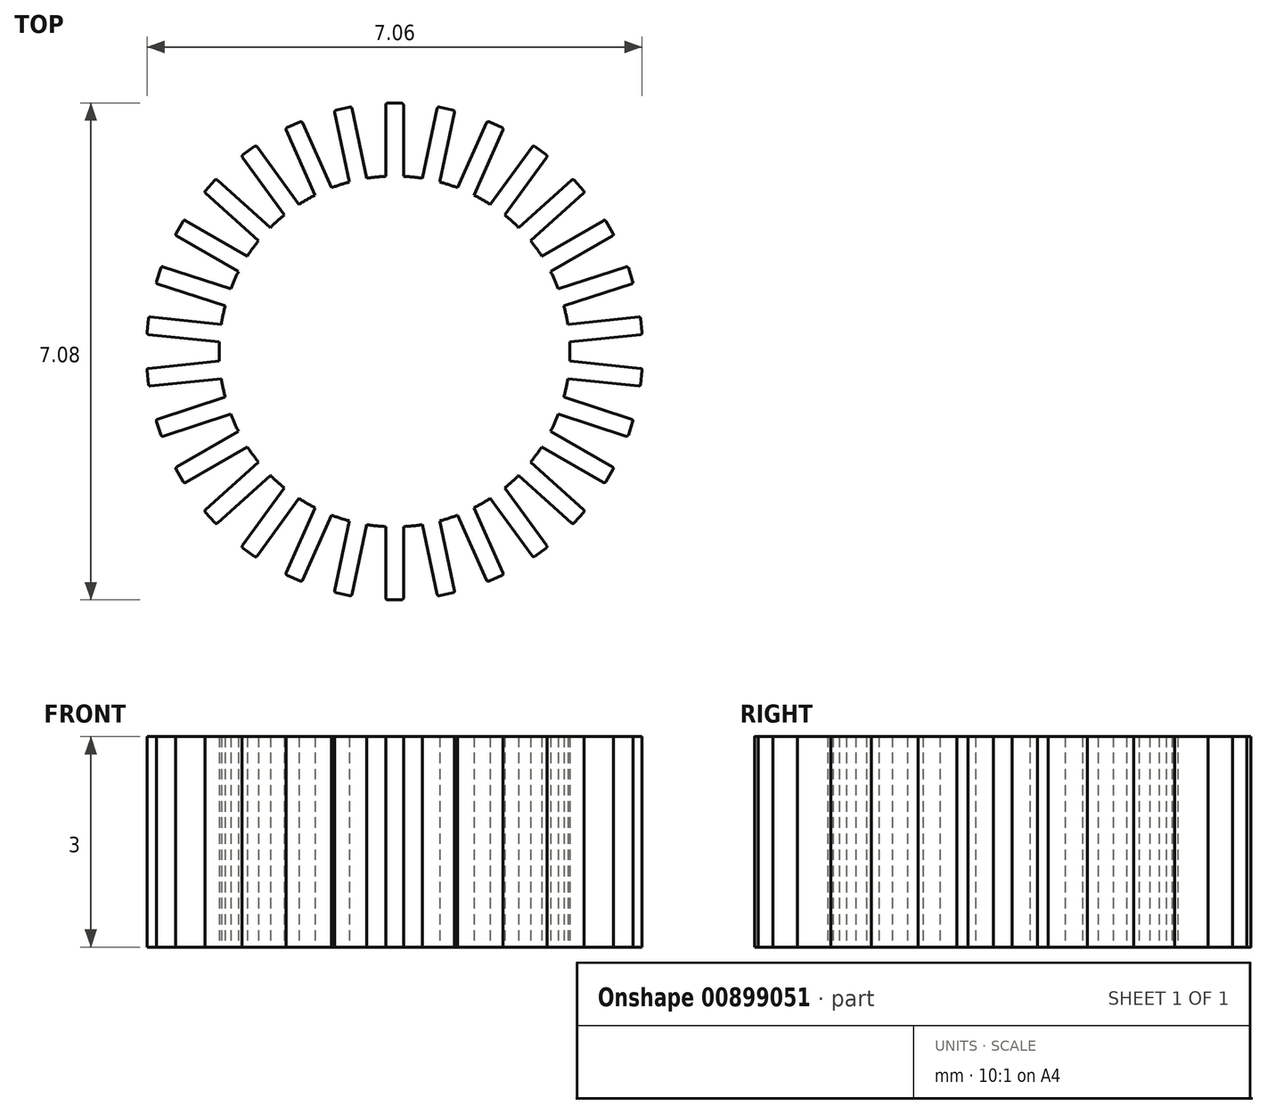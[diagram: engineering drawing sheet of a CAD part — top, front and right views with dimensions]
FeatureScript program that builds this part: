
annotation { "Feature Type Name" : "Feature", "Feature Type Description" : "" }
export const myFeature = defineFeature(function(context is Context, id is Id, definition is map)
    precondition{}
    {
        {
            var Q0;
            Q0=qCreatedBy(makeId("Top.planeOp"),FACE);
            var sketch = newSketch(context, id + "F0", { "sketchPlane" : qUnion([Q0])});
            skCircle(sketch, "E0", {"center": v(0, 0) * mm, "radius": 2.5 * mm});
            skLineSegment(sketch, "E1", {"start": v(0, 3.54) * mm, "end": v(-0.1, 3.54) * mm});
            skLineSegment(sketch, "E2", {"start": v(0, 3.54) * mm, "end": v(0.1, 3.54) * mm});
            skLineSegment(sketch, "E3", {"start": v(-0.13, 3.51) * mm, "end": v(-0.13, 2.5) * mm});
            skLineSegment(sketch, "E4", {"start": v(0.13, 3.51) * mm, "end": v(0.13, 2.5) * mm});
            skPoint(sketch, "E5.visualSharp", {"position": v(-0.13, 3.54) * mm});
            skArc(sketch, "E5.filletArc", {"start": v(-0.1, 3.54) * mm, "mid": v(-0.12, 3.53) * mm, "end": v(-0.13, 3.51) * mm});
            skPoint(sketch, "E6.visualSharp", {"position": v(0.13, 3.54) * mm});
            skArc(sketch, "E6.filletArc", {"start": v(0.13, 3.51) * mm, "mid": v(0.12, 3.53) * mm, "end": v(0.1, 3.54) * mm});
            skLineSegment(sketch, "E7", {"start": v(-0.13, 2.5) * mm, "end": v(-0.05, 2.5) * mm});
            skLineSegment(sketch, "E8.1.0", {"start": v(-2.98, -1.87) * mm, "end": v(-2.1, -1.36) * mm});
            skLineSegment(sketch, "E8.2.0", {"start": v(3.1, -1.65) * mm, "end": v(2.23, -1.14) * mm});
            skArc(sketch, "E9.1.0", {"start": v(-0.84, 3.44) * mm, "mid": v(-0.85, 3.43) * mm, "end": v(-0.85, 3.4) * mm});
            skLineSegment(sketch, "E9.1.1", {"start": v(-0.74, 3.46) * mm, "end": v(-0.84, 3.44) * mm});
            skLineSegment(sketch, "E9.1.2", {"start": v(-0.74, 3.46) * mm, "end": v(-0.64, 3.48) * mm});
            skArc(sketch, "E9.1.3", {"start": v(-0.6, 3.46) * mm, "mid": v(-0.62, 3.48) * mm, "end": v(-0.64, 3.48) * mm});
            skLineSegment(sketch, "E9.1.4", {"start": v(-0.6, 3.46) * mm, "end": v(-0.4, 2.47) * mm});
            skLineSegment(sketch, "E9.1.5", {"start": v(-0.85, 3.4) * mm, "end": v(-0.64, 2.42) * mm});
            skArc(sketch, "E9.2.0", {"start": v(-1.53, 3.2) * mm, "mid": v(-1.55, 3.18) * mm, "end": v(-1.54, 3.16) * mm});
            skLineSegment(sketch, "E9.2.1", {"start": v(-1.44, 3.23) * mm, "end": v(-1.53, 3.2) * mm});
            skLineSegment(sketch, "E9.2.2", {"start": v(-1.44, 3.23) * mm, "end": v(-1.35, 3.27) * mm});
            skArc(sketch, "E9.2.3", {"start": v(-1.31, 3.26) * mm, "mid": v(-1.33, 3.27) * mm, "end": v(-1.35, 3.27) * mm});
            skLineSegment(sketch, "E9.2.4", {"start": v(-1.31, 3.26) * mm, "end": v(-0.9, 2.33) * mm});
            skLineSegment(sketch, "E9.2.5", {"start": v(-1.54, 3.16) * mm, "end": v(-1.13, 2.23) * mm});
            skArc(sketch, "E9.3.0", {"start": v(-2.16, 2.8) * mm, "mid": v(-2.17, 2.79) * mm, "end": v(-2.17, 2.77) * mm});
            skLineSegment(sketch, "E9.3.1", {"start": v(-2.08, 2.86) * mm, "end": v(-2.16, 2.8) * mm});
            skLineSegment(sketch, "E9.3.2", {"start": v(-2.08, 2.86) * mm, "end": v(-2, 2.92) * mm});
            skArc(sketch, "E9.3.3", {"start": v(-1.96, 2.92) * mm, "mid": v(-1.98, 2.93) * mm, "end": v(-2, 2.92) * mm});
            skLineSegment(sketch, "E9.3.4", {"start": v(-1.96, 2.92) * mm, "end": v(-1.36, 2.1) * mm});
            skLineSegment(sketch, "E9.3.5", {"start": v(-2.17, 2.77) * mm, "end": v(-1.57, 1.95) * mm});
            skArc(sketch, "E9.4.0", {"start": v(-2.7, 2.3) * mm, "mid": v(-2.7, 2.27) * mm, "end": v(-2.7, 2.26) * mm});
            skLineSegment(sketch, "E9.4.1", {"start": v(-2.63, 2.37) * mm, "end": v(-2.7, 2.3) * mm});
            skLineSegment(sketch, "E9.4.2", {"start": v(-2.63, 2.37) * mm, "end": v(-2.56, 2.44) * mm});
            skArc(sketch, "E9.4.3", {"start": v(-2.53, 2.44) * mm, "mid": v(-2.54, 2.45) * mm, "end": v(-2.56, 2.44) * mm});
            skLineSegment(sketch, "E9.4.4", {"start": v(-2.53, 2.44) * mm, "end": v(-1.77, 1.77) * mm});
            skLineSegment(sketch, "E9.4.5", {"start": v(-2.7, 2.26) * mm, "end": v(-1.94, 1.58) * mm});
            skArc(sketch, "E9.5.0", {"start": v(-3.11, 1.68) * mm, "mid": v(-3.12, 1.66) * mm, "end": v(-3.1, 1.65) * mm});
            skLineSegment(sketch, "E9.5.1", {"start": v(-3.06, 1.77) * mm, "end": v(-3.11, 1.68) * mm});
            skLineSegment(sketch, "E9.5.2", {"start": v(-3.06, 1.77) * mm, "end": v(-3.01, 1.86) * mm});
            skArc(sketch, "E9.5.3", {"start": v(-2.98, 1.87) * mm, "mid": v(-3, 1.87) * mm, "end": v(-3.01, 1.86) * mm});
            skLineSegment(sketch, "E9.5.4", {"start": v(-2.98, 1.87) * mm, "end": v(-2.1, 1.36) * mm});
            skLineSegment(sketch, "E9.5.5", {"start": v(-3.1, 1.65) * mm, "end": v(-2.23, 1.14) * mm});
            skArc(sketch, "E9.6.0", {"start": v(-3.4, 1) * mm, "mid": v(-3.4, 0.98) * mm, "end": v(-3.38, 0.96) * mm});
            skLineSegment(sketch, "E9.6.1", {"start": v(-3.37, 1.1) * mm, "end": v(-3.4, 1) * mm});
            skLineSegment(sketch, "E9.6.2", {"start": v(-3.37, 1.1) * mm, "end": v(-3.33, 1.19) * mm});
            skArc(sketch, "E9.6.3", {"start": v(-3.3, 1.2) * mm, "mid": v(-3.32, 1.2) * mm, "end": v(-3.33, 1.19) * mm});
            skLineSegment(sketch, "E9.6.4", {"start": v(-3.3, 1.2) * mm, "end": v(-2.34, 0.9) * mm});
            skLineSegment(sketch, "E9.6.5", {"start": v(-3.38, 0.96) * mm, "end": v(-2.41, 0.65) * mm});
            skArc(sketch, "E9.7.0", {"start": v(-3.53, 0.27) * mm, "mid": v(-3.52, 0.25) * mm, "end": v(-3.5, 0.24) * mm});
            skLineSegment(sketch, "E9.7.1", {"start": v(-3.52, 0.37) * mm, "end": v(-3.53, 0.27) * mm});
            skLineSegment(sketch, "E9.7.2", {"start": v(-3.52, 0.37) * mm, "end": v(-3.5, 0.47) * mm});
            skArc(sketch, "E9.7.3", {"start": v(-3.48, 0.5) * mm, "mid": v(-3.5, 0.49) * mm, "end": v(-3.5, 0.47) * mm});
            skLineSegment(sketch, "E9.7.4", {"start": v(-3.48, 0.5) * mm, "end": v(-2.47, 0.39) * mm});
            skLineSegment(sketch, "E9.7.5", {"start": v(-3.5, 0.24) * mm, "end": v(-2.5, 0.13) * mm});
            skArc(sketch, "E9.8.0", {"start": v(-3.5, -0.47) * mm, "mid": v(-3.5, -0.49) * mm, "end": v(-3.48, -0.5) * mm});
            skLineSegment(sketch, "E9.8.1", {"start": v(-3.52, -0.37) * mm, "end": v(-3.5, -0.47) * mm});
            skLineSegment(sketch, "E9.8.2", {"start": v(-3.52, -0.37) * mm, "end": v(-3.53, -0.27) * mm});
            skArc(sketch, "E9.8.3", {"start": v(-3.5, -0.24) * mm, "mid": v(-3.52, -0.25) * mm, "end": v(-3.53, -0.27) * mm});
            skLineSegment(sketch, "E9.8.4", {"start": v(-3.5, -0.24) * mm, "end": v(-2.5, -0.13) * mm});
            skLineSegment(sketch, "E9.8.5", {"start": v(-3.48, -0.5) * mm, "end": v(-2.47, -0.39) * mm});
            skArc(sketch, "E9.9.0", {"start": v(-3.33, -1.19) * mm, "mid": v(-3.32, -1.2) * mm, "end": v(-3.3, -1.2) * mm});
            skLineSegment(sketch, "E9.9.1", {"start": v(-3.37, -1.1) * mm, "end": v(-3.33, -1.19) * mm});
            skLineSegment(sketch, "E9.9.2", {"start": v(-3.37, -1.1) * mm, "end": v(-3.4, -1) * mm});
            skArc(sketch, "E9.9.3", {"start": v(-3.38, -0.96) * mm, "mid": v(-3.4, -0.98) * mm, "end": v(-3.4, -1) * mm});
            skLineSegment(sketch, "E9.9.4", {"start": v(-3.38, -0.96) * mm, "end": v(-2.41, -0.65) * mm});
            skLineSegment(sketch, "E9.9.5", {"start": v(-3.3, -1.2) * mm, "end": v(-2.34, -0.9) * mm});
            skArc(sketch, "E9.10.0", {"start": v(-3.01, -1.86) * mm, "mid": v(-3, -1.87) * mm, "end": v(-2.98, -1.87) * mm});
            skLineSegment(sketch, "E9.10.1", {"start": v(-3.06, -1.77) * mm, "end": v(-3.01, -1.86) * mm});
            skLineSegment(sketch, "E9.10.2", {"start": v(-3.06, -1.77) * mm, "end": v(-3.11, -1.68) * mm});
            skArc(sketch, "E9.10.3", {"start": v(-3.1, -1.65) * mm, "mid": v(-3.12, -1.66) * mm, "end": v(-3.11, -1.68) * mm});
            skLineSegment(sketch, "E9.10.4", {"start": v(-3.1, -1.65) * mm, "end": v(-2.23, -1.14) * mm});
            skArc(sketch, "E9.11.0", {"start": v(-2.56, -2.44) * mm, "mid": v(-2.54, -2.45) * mm, "end": v(-2.53, -2.44) * mm});
            skLineSegment(sketch, "E9.11.1", {"start": v(-2.63, -2.37) * mm, "end": v(-2.56, -2.44) * mm});
            skLineSegment(sketch, "E9.11.2", {"start": v(-2.63, -2.37) * mm, "end": v(-2.7, -2.3) * mm});
            skArc(sketch, "E9.11.3", {"start": v(-2.7, -2.26) * mm, "mid": v(-2.7, -2.27) * mm, "end": v(-2.7, -2.3) * mm});
            skLineSegment(sketch, "E9.11.4", {"start": v(-2.7, -2.26) * mm, "end": v(-1.94, -1.58) * mm});
            skLineSegment(sketch, "E9.11.5", {"start": v(-2.53, -2.44) * mm, "end": v(-1.77, -1.77) * mm});
            skArc(sketch, "E9.12.0", {"start": v(-2, -2.92) * mm, "mid": v(-1.98, -2.93) * mm, "end": v(-1.96, -2.92) * mm});
            skLineSegment(sketch, "E9.12.1", {"start": v(-2.08, -2.86) * mm, "end": v(-2, -2.92) * mm});
            skLineSegment(sketch, "E9.12.2", {"start": v(-2.08, -2.86) * mm, "end": v(-2.16, -2.8) * mm});
            skArc(sketch, "E9.12.3", {"start": v(-2.17, -2.77) * mm, "mid": v(-2.17, -2.79) * mm, "end": v(-2.16, -2.8) * mm});
            skLineSegment(sketch, "E9.12.4", {"start": v(-2.17, -2.77) * mm, "end": v(-1.57, -1.95) * mm});
            skLineSegment(sketch, "E9.12.5", {"start": v(-1.96, -2.92) * mm, "end": v(-1.36, -2.1) * mm});
            skArc(sketch, "E9.13.0", {"start": v(-1.35, -3.27) * mm, "mid": v(-1.33, -3.27) * mm, "end": v(-1.31, -3.26) * mm});
            skLineSegment(sketch, "E9.13.1", {"start": v(-1.44, -3.23) * mm, "end": v(-1.35, -3.27) * mm});
            skLineSegment(sketch, "E9.13.2", {"start": v(-1.44, -3.23) * mm, "end": v(-1.53, -3.2) * mm});
            skArc(sketch, "E9.13.3", {"start": v(-1.54, -3.16) * mm, "mid": v(-1.55, -3.18) * mm, "end": v(-1.53, -3.2) * mm});
            skLineSegment(sketch, "E9.13.4", {"start": v(-1.54, -3.16) * mm, "end": v(-1.13, -2.23) * mm});
            skLineSegment(sketch, "E9.13.5", {"start": v(-1.31, -3.26) * mm, "end": v(-0.9, -2.33) * mm});
            skArc(sketch, "E9.14.0", {"start": v(-0.64, -3.48) * mm, "mid": v(-0.62, -3.48) * mm, "end": v(-0.6, -3.46) * mm});
            skLineSegment(sketch, "E9.14.1", {"start": v(-0.74, -3.46) * mm, "end": v(-0.64, -3.48) * mm});
            skLineSegment(sketch, "E9.14.2", {"start": v(-0.74, -3.46) * mm, "end": v(-0.84, -3.44) * mm});
            skArc(sketch, "E9.14.3", {"start": v(-0.85, -3.4) * mm, "mid": v(-0.85, -3.43) * mm, "end": v(-0.84, -3.44) * mm});
            skLineSegment(sketch, "E9.14.4", {"start": v(-0.85, -3.4) * mm, "end": v(-0.64, -2.42) * mm});
            skLineSegment(sketch, "E9.14.5", {"start": v(-0.6, -3.46) * mm, "end": v(-0.4, -2.47) * mm});
            skArc(sketch, "E9.15.0", {"start": v(0.1, -3.54) * mm, "mid": v(0.12, -3.53) * mm, "end": v(0.13, -3.51) * mm});
            skLineSegment(sketch, "E9.15.1", {"start": v(0, -3.54) * mm, "end": v(0.1, -3.54) * mm});
            skLineSegment(sketch, "E9.15.2", {"start": v(0, -3.54) * mm, "end": v(-0.1, -3.54) * mm});
            skArc(sketch, "E9.15.3", {"start": v(-0.13, -3.51) * mm, "mid": v(-0.12, -3.53) * mm, "end": v(-0.1, -3.54) * mm});
            skLineSegment(sketch, "E9.15.4", {"start": v(-0.13, -3.51) * mm, "end": v(-0.13, -2.5) * mm});
            skLineSegment(sketch, "E9.15.5", {"start": v(0.13, -3.51) * mm, "end": v(0.13, -2.5) * mm});
            skArc(sketch, "E9.16.0", {"start": v(0.84, -3.44) * mm, "mid": v(0.85, -3.43) * mm, "end": v(0.85, -3.4) * mm});
            skLineSegment(sketch, "E9.16.1", {"start": v(0.74, -3.46) * mm, "end": v(0.84, -3.44) * mm});
            skLineSegment(sketch, "E9.16.2", {"start": v(0.74, -3.46) * mm, "end": v(0.64, -3.48) * mm});
            skArc(sketch, "E9.16.3", {"start": v(0.6, -3.46) * mm, "mid": v(0.62, -3.48) * mm, "end": v(0.64, -3.48) * mm});
            skLineSegment(sketch, "E9.16.4", {"start": v(0.6, -3.46) * mm, "end": v(0.4, -2.47) * mm});
            skLineSegment(sketch, "E9.16.5", {"start": v(0.85, -3.4) * mm, "end": v(0.64, -2.42) * mm});
            skArc(sketch, "E9.17.0", {"start": v(1.53, -3.2) * mm, "mid": v(1.55, -3.18) * mm, "end": v(1.54, -3.16) * mm});
            skLineSegment(sketch, "E9.17.1", {"start": v(1.44, -3.23) * mm, "end": v(1.53, -3.2) * mm});
            skLineSegment(sketch, "E9.17.2", {"start": v(1.44, -3.23) * mm, "end": v(1.35, -3.27) * mm});
            skArc(sketch, "E9.17.3", {"start": v(1.31, -3.26) * mm, "mid": v(1.33, -3.27) * mm, "end": v(1.35, -3.27) * mm});
            skLineSegment(sketch, "E9.17.4", {"start": v(1.31, -3.26) * mm, "end": v(0.9, -2.33) * mm});
            skLineSegment(sketch, "E9.17.5", {"start": v(1.54, -3.16) * mm, "end": v(1.13, -2.23) * mm});
            skArc(sketch, "E9.18.0", {"start": v(2.16, -2.8) * mm, "mid": v(2.17, -2.79) * mm, "end": v(2.17, -2.77) * mm});
            skLineSegment(sketch, "E9.18.1", {"start": v(2.08, -2.86) * mm, "end": v(2.16, -2.8) * mm});
            skLineSegment(sketch, "E9.18.2", {"start": v(2.08, -2.86) * mm, "end": v(2, -2.92) * mm});
            skArc(sketch, "E9.18.3", {"start": v(1.96, -2.92) * mm, "mid": v(1.98, -2.93) * mm, "end": v(2, -2.92) * mm});
            skLineSegment(sketch, "E9.18.4", {"start": v(1.96, -2.92) * mm, "end": v(1.36, -2.1) * mm});
            skLineSegment(sketch, "E9.18.5", {"start": v(2.17, -2.77) * mm, "end": v(1.57, -1.95) * mm});
            skArc(sketch, "E9.19.0", {"start": v(2.7, -2.3) * mm, "mid": v(2.7, -2.27) * mm, "end": v(2.7, -2.26) * mm});
            skLineSegment(sketch, "E9.19.1", {"start": v(2.63, -2.37) * mm, "end": v(2.7, -2.3) * mm});
            skLineSegment(sketch, "E9.19.2", {"start": v(2.63, -2.37) * mm, "end": v(2.56, -2.44) * mm});
            skArc(sketch, "E9.19.3", {"start": v(2.53, -2.44) * mm, "mid": v(2.54, -2.45) * mm, "end": v(2.56, -2.44) * mm});
            skLineSegment(sketch, "E9.19.4", {"start": v(2.53, -2.44) * mm, "end": v(1.77, -1.77) * mm});
            skLineSegment(sketch, "E9.19.5", {"start": v(2.7, -2.26) * mm, "end": v(1.94, -1.58) * mm});
            skArc(sketch, "E9.20.0", {"start": v(3.11, -1.68) * mm, "mid": v(3.12, -1.66) * mm, "end": v(3.1, -1.65) * mm});
            skLineSegment(sketch, "E9.20.1", {"start": v(3.06, -1.77) * mm, "end": v(3.11, -1.68) * mm});
            skLineSegment(sketch, "E9.20.2", {"start": v(3.06, -1.77) * mm, "end": v(3.01, -1.86) * mm});
            skArc(sketch, "E9.20.3", {"start": v(2.98, -1.87) * mm, "mid": v(3, -1.87) * mm, "end": v(3.01, -1.86) * mm});
            skLineSegment(sketch, "E9.20.4", {"start": v(2.98, -1.87) * mm, "end": v(2.1, -1.36) * mm});
            skArc(sketch, "E9.21.0", {"start": v(3.4, -1) * mm, "mid": v(3.4, -0.98) * mm, "end": v(3.38, -0.96) * mm});
            skLineSegment(sketch, "E9.21.1", {"start": v(3.37, -1.1) * mm, "end": v(3.4, -1) * mm});
            skLineSegment(sketch, "E9.21.2", {"start": v(3.37, -1.1) * mm, "end": v(3.33, -1.19) * mm});
            skArc(sketch, "E9.21.3", {"start": v(3.3, -1.2) * mm, "mid": v(3.32, -1.2) * mm, "end": v(3.33, -1.19) * mm});
            skLineSegment(sketch, "E9.21.4", {"start": v(3.3, -1.2) * mm, "end": v(2.34, -0.9) * mm});
            skLineSegment(sketch, "E9.21.5", {"start": v(3.38, -0.96) * mm, "end": v(2.41, -0.65) * mm});
            skArc(sketch, "E9.22.0", {"start": v(3.53, -0.27) * mm, "mid": v(3.52, -0.25) * mm, "end": v(3.5, -0.24) * mm});
            skLineSegment(sketch, "E9.22.1", {"start": v(3.52, -0.37) * mm, "end": v(3.53, -0.27) * mm});
            skLineSegment(sketch, "E9.22.2", {"start": v(3.52, -0.37) * mm, "end": v(3.5, -0.47) * mm});
            skArc(sketch, "E9.22.3", {"start": v(3.48, -0.5) * mm, "mid": v(3.5, -0.49) * mm, "end": v(3.5, -0.47) * mm});
            skLineSegment(sketch, "E9.22.4", {"start": v(3.48, -0.5) * mm, "end": v(2.47, -0.39) * mm});
            skLineSegment(sketch, "E9.22.5", {"start": v(3.5, -0.24) * mm, "end": v(2.5, -0.13) * mm});
            skArc(sketch, "E9.23.0", {"start": v(3.5, 0.47) * mm, "mid": v(3.5, 0.49) * mm, "end": v(3.48, 0.5) * mm});
            skLineSegment(sketch, "E9.23.1", {"start": v(3.52, 0.37) * mm, "end": v(3.5, 0.47) * mm});
            skLineSegment(sketch, "E9.23.2", {"start": v(3.52, 0.37) * mm, "end": v(3.53, 0.27) * mm});
            skArc(sketch, "E9.23.3", {"start": v(3.5, 0.24) * mm, "mid": v(3.52, 0.25) * mm, "end": v(3.53, 0.27) * mm});
            skLineSegment(sketch, "E9.23.4", {"start": v(3.5, 0.24) * mm, "end": v(2.5, 0.13) * mm});
            skLineSegment(sketch, "E9.23.5", {"start": v(3.48, 0.5) * mm, "end": v(2.47, 0.39) * mm});
            skArc(sketch, "E9.24.0", {"start": v(3.33, 1.19) * mm, "mid": v(3.32, 1.2) * mm, "end": v(3.3, 1.2) * mm});
            skLineSegment(sketch, "E9.24.1", {"start": v(3.37, 1.1) * mm, "end": v(3.33, 1.19) * mm});
            skLineSegment(sketch, "E9.24.2", {"start": v(3.37, 1.1) * mm, "end": v(3.4, 1) * mm});
            skArc(sketch, "E9.24.3", {"start": v(3.38, 0.96) * mm, "mid": v(3.4, 0.98) * mm, "end": v(3.4, 1) * mm});
            skLineSegment(sketch, "E9.24.4", {"start": v(3.38, 0.96) * mm, "end": v(2.41, 0.65) * mm});
            skLineSegment(sketch, "E9.24.5", {"start": v(3.3, 1.2) * mm, "end": v(2.34, 0.9) * mm});
            skArc(sketch, "E9.25.0", {"start": v(3.01, 1.86) * mm, "mid": v(3, 1.87) * mm, "end": v(2.98, 1.87) * mm});
            skLineSegment(sketch, "E9.25.1", {"start": v(3.06, 1.77) * mm, "end": v(3.01, 1.86) * mm});
            skLineSegment(sketch, "E9.25.2", {"start": v(3.06, 1.77) * mm, "end": v(3.11, 1.68) * mm});
            skArc(sketch, "E9.25.3", {"start": v(3.1, 1.65) * mm, "mid": v(3.12, 1.66) * mm, "end": v(3.11, 1.68) * mm});
            skLineSegment(sketch, "E9.25.4", {"start": v(3.1, 1.65) * mm, "end": v(2.23, 1.14) * mm});
            skLineSegment(sketch, "E9.25.5", {"start": v(2.98, 1.87) * mm, "end": v(2.1, 1.36) * mm});
            skArc(sketch, "E9.26.0", {"start": v(2.56, 2.44) * mm, "mid": v(2.54, 2.45) * mm, "end": v(2.53, 2.44) * mm});
            skLineSegment(sketch, "E9.26.1", {"start": v(2.63, 2.37) * mm, "end": v(2.56, 2.44) * mm});
            skLineSegment(sketch, "E9.26.2", {"start": v(2.63, 2.37) * mm, "end": v(2.7, 2.3) * mm});
            skArc(sketch, "E9.26.3", {"start": v(2.7, 2.26) * mm, "mid": v(2.7, 2.27) * mm, "end": v(2.7, 2.3) * mm});
            skLineSegment(sketch, "E9.26.4", {"start": v(2.7, 2.26) * mm, "end": v(1.94, 1.58) * mm});
            skLineSegment(sketch, "E9.26.5", {"start": v(2.53, 2.44) * mm, "end": v(1.77, 1.77) * mm});
            skArc(sketch, "E9.27.0", {"start": v(2, 2.92) * mm, "mid": v(1.98, 2.93) * mm, "end": v(1.96, 2.92) * mm});
            skLineSegment(sketch, "E9.27.1", {"start": v(2.08, 2.86) * mm, "end": v(2, 2.92) * mm});
            skLineSegment(sketch, "E9.27.2", {"start": v(2.08, 2.86) * mm, "end": v(2.16, 2.8) * mm});
            skArc(sketch, "E9.27.3", {"start": v(2.17, 2.77) * mm, "mid": v(2.17, 2.79) * mm, "end": v(2.16, 2.8) * mm});
            skLineSegment(sketch, "E9.27.4", {"start": v(2.17, 2.77) * mm, "end": v(1.57, 1.95) * mm});
            skLineSegment(sketch, "E9.27.5", {"start": v(1.96, 2.92) * mm, "end": v(1.36, 2.1) * mm});
            skArc(sketch, "E9.28.0", {"start": v(1.35, 3.27) * mm, "mid": v(1.33, 3.27) * mm, "end": v(1.31, 3.26) * mm});
            skLineSegment(sketch, "E9.28.1", {"start": v(1.44, 3.23) * mm, "end": v(1.35, 3.27) * mm});
            skLineSegment(sketch, "E9.28.2", {"start": v(1.44, 3.23) * mm, "end": v(1.53, 3.2) * mm});
            skArc(sketch, "E9.28.3", {"start": v(1.54, 3.16) * mm, "mid": v(1.55, 3.18) * mm, "end": v(1.53, 3.2) * mm});
            skLineSegment(sketch, "E9.28.4", {"start": v(1.54, 3.16) * mm, "end": v(1.13, 2.23) * mm});
            skLineSegment(sketch, "E9.28.5", {"start": v(1.31, 3.26) * mm, "end": v(0.9, 2.33) * mm});
            skArc(sketch, "E9.29.0", {"start": v(0.64, 3.48) * mm, "mid": v(0.62, 3.48) * mm, "end": v(0.6, 3.46) * mm});
            skLineSegment(sketch, "E9.29.1", {"start": v(0.74, 3.46) * mm, "end": v(0.64, 3.48) * mm});
            skLineSegment(sketch, "E9.29.2", {"start": v(0.74, 3.46) * mm, "end": v(0.84, 3.44) * mm});
            skArc(sketch, "E9.29.3", {"start": v(0.85, 3.4) * mm, "mid": v(0.85, 3.43) * mm, "end": v(0.84, 3.44) * mm});
            skLineSegment(sketch, "E9.29.4", {"start": v(0.85, 3.4) * mm, "end": v(0.64, 2.42) * mm});
            skLineSegment(sketch, "E9.29.5", {"start": v(0.6, 3.46) * mm, "end": v(0.4, 2.47) * mm});
            skSolve(sketch);
        }
        {
            var Q0;
            Q0 = qSketchRegion(id + "F0", true);
            extrude(context, id + "F1", {"entities" : qUnion([Q0]), "depth" : 3 * mm, "offsetDistance" : 25.4 * mm});
        }
    });
